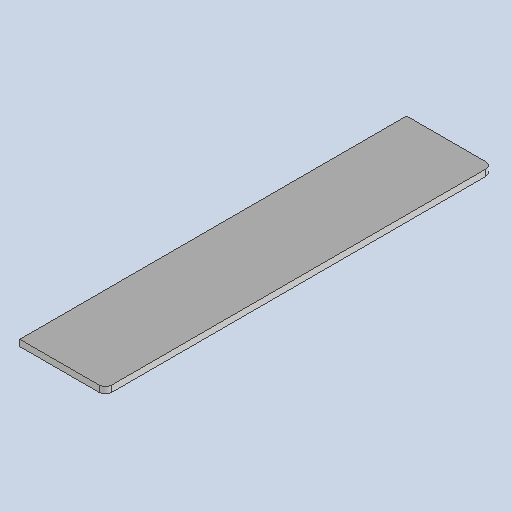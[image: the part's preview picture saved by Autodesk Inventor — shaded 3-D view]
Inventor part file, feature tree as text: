
AUTODESK INVENTOR PART (.ipt)
format: ipt  version: 2025 (Build 290162010, 162A)  size: 200,704 bytes
history: native  units: mm
features: other x4, sketch x2, sheet_metal_op x1, chamfer x1
ambient origin geometry x8: Origin, YZ Plane, XZ Plane, XY Plane, X Axis, Y Axis, Z Axis, Center Point
bodies: Solid1 (feature_tree)
feature tree (8):
  sheet_metal_op  "Face1"
  other  "Mark1"
  other  "A-Side Definition"
  chamfer  "Corner Round1"
  sketch  "Sketch1"  dims[d0=27.0mm]
  other  "Plate1"
  sketch  "Sketch2"  dims[d1=122.0mm d2=2.0mm d6=200.0mm d9=20.0mm d10=20.0mm d11=20.0mm d12=11.0mm d13=102.0mm d14=2.0mm d15=15.0mm]
  other  "Definition1"
